# Revit family: J2 PET Felt Horizon Cloud Grid
name_source: partatom
category: Specialty Equipment
units: mm (PartAtom-declared; Revit-internal decimal feet)

## family parameters
Always vertical = Yes
Cut with Voids When Loaded = No
Part Type = Normal
Room Calculation Point = No
Round Connector Dimension = Use Diameter
Shared = No
Work Plane-Based = No

## types (2) — shared parameters
Baffle Height (Max. 3'-11") = 0' - 11"
Default Elevation = 0' - 0"
End Spacing "X" = 0' - 6"
End Spacing "Y" = 0' - 6"
Manufacturer = J2 Systems
Model = Horizon Cloud Grid
Product Line = Ceiling System
Release Date = 2019
Style Number = CSCGHO
URL = https://www.j2systems.net

## per-type parameters (varying)
| type | Baffles in "X" direction | Baffles in "Y" direction | Nominal Length "X" (Max. 8') | Nominal Width "Y" (Max. 8') |
| Horizon Cloud Grid 8'x8' | 8 | 8 | 8' - 0" | 8' - 0" |
| Horizon Cloud Grid 4'x4' | 4 | 4 | 4' - 0" | 4' - 0" |

## geometry (parser evidence)
native form markers: Sweep x7
no freeform markers — native parametric forms only
